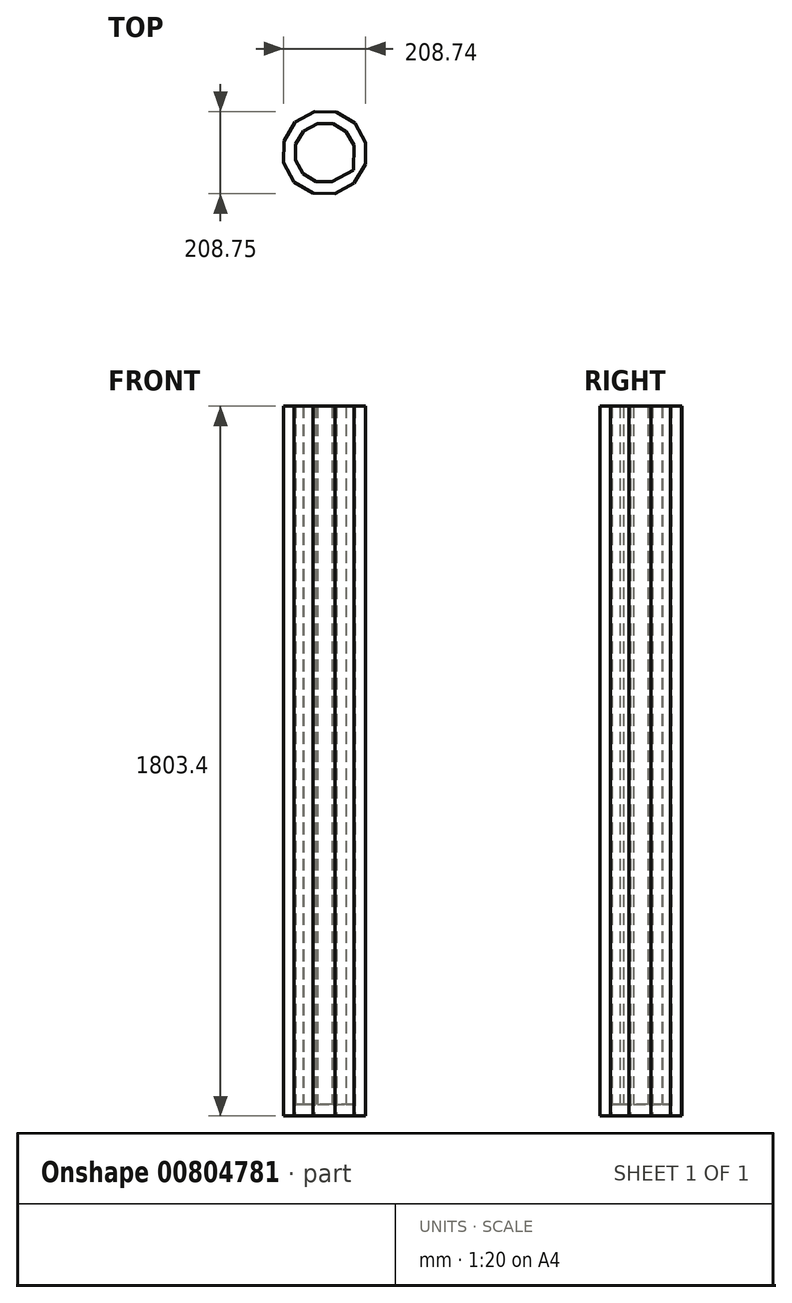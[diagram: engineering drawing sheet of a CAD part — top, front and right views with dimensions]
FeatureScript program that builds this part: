
annotation { "Feature Type Name" : "Feature", "Feature Type Description" : "" }
export const myFeature = defineFeature(function(context is Context, id is Id, definition is map)
    precondition{}
    {
        {
            var Q0;
            Q0=qCreatedBy(makeId("Top.planeOp"),FACE);
            var sketch = newSketch(context, id + "F0", { "sketchPlane" : qUnion([Q0])});
            skCircle(sketch, "E0.cCircle", {"center": v(-132.73, 7.93) * mm, "radius": 103.9 * mm, "construction": true});
            skLineSegment(sketch, "E0.0", {"start": v(-29.35, -21.76) * mm, "end": v(-58.05, -69.47) * mm});
            skLineSegment(sketch, "E0.1", {"start": v(-58.05, -69.47) * mm, "end": v(-106.76, -96.44) * mm});
            skLineSegment(sketch, "E0.2", {"start": v(-106.76, -96.44) * mm, "end": v(-162.42, -95.44) * mm});
            skLineSegment(sketch, "E0.3", {"start": v(-162.42, -95.44) * mm, "end": v(-210.13, -66.75) * mm});
            skLineSegment(sketch, "E0.4", {"start": v(-210.13, -66.75) * mm, "end": v(-237.1, -18.04) * mm});
            skLineSegment(sketch, "E0.5", {"start": v(-237.1, -18.04) * mm, "end": v(-236.1, 37.63) * mm});
            skLineSegment(sketch, "E0.6", {"start": v(-236.1, 37.63) * mm, "end": v(-207.41, 85.34) * mm});
            skLineSegment(sketch, "E0.7", {"start": v(-207.41, 85.34) * mm, "end": v(-158.7, 112.3) * mm});
            skLineSegment(sketch, "E0.8", {"start": v(-158.7, 112.3) * mm, "end": v(-103.04, 111.31) * mm});
            skLineSegment(sketch, "E0.9", {"start": v(-103.04, 111.31) * mm, "end": v(-55.33, 82.61) * mm});
            skLineSegment(sketch, "E0.10", {"start": v(-55.33, 82.61) * mm, "end": v(-28.36, 33.9) * mm});
            skLineSegment(sketch, "E0.11", {"start": v(-28.36, 33.9) * mm, "end": v(-29.35, -21.76) * mm});
            skPoint(sketch, "E0.0.midPoint", {"position": v(-43.7, -45.61) * mm});
            skSolve(sketch);
        }
        {
            var Q0;
            Q0=makeQuery(id+"F0.imprint","IMPRINT",FACE,{"disambiguationData":[TD([[makeQuery(id+"F0.imprint","IMPRINT",EDGE,{"derivedFrom":sQuery(id+"F0.wireOp",EDGE,"E0.0")}),-1.0]])]});
            extrude(context, id + "F1", {"entities" : qUnion([Q0]), "depth" : 1803.4 * mm, "offsetDistance" : 25.4 * mm});
        }
        {
            var Q0;
            Q0=makeQuery(id+"F1.opExtrude","SWEPT_FACE",FACE,{"disambiguationData":[OSD([sQuery(id+"F0.wireOp",EDGE,"E0.0")])]});
            var Q1;
            Q1=makeQuery(id+"F1.opExtrude","CAP_FACE",FACE,{"disambiguationData":[OSD([sQuery(id+"F0.wireOp",EDGE,"E0.0"),sQuery(id+"F0.wireOp",EDGE,"E0.1"),sQuery(id+"F0.wireOp",EDGE,"E0.2"),sQuery(id+"F0.wireOp",EDGE,"E0.3"),sQuery(id+"F0.wireOp",EDGE,"E0.4"),sQuery(id+"F0.wireOp",EDGE,"E0.5"),sQuery(id+"F0.wireOp",EDGE,"E0.6"),sQuery(id+"F0.wireOp",EDGE,"E0.7"),sQuery(id+"F0.wireOp",EDGE,"E0.8"),sQuery(id+"F0.wireOp",EDGE,"E0.9"),sQuery(id+"F0.wireOp",EDGE,"E0.10"),sQuery(id+"F0.wireOp",EDGE,"E0.11")])],"isStart":false});
            shell(context, id + "F2", {"entities" : qUnion([Q0, Q1]), "thickness" : 30 * mm});
        }
    });
